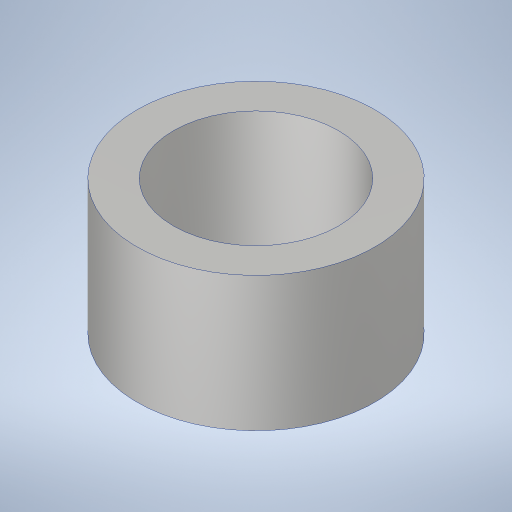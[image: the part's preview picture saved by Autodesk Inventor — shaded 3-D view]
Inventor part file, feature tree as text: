
AUTODESK INVENTOR PART (.ipt)
format: ipt  version: 2023.4 (Build 274418000, 418)  size: 215,552 bytes
history: native  units: in
note: dims shown in document units (in); Inventor stores cm internally (conversion verified against a paired STEP export)
features: extrude x1, sketch x1
ambient origin geometry x8: Origin, YZ Plane, XZ Plane, XY Plane, X Axis, Y Axis, Z Axis, Center Point
bodies: Solid1 (feature_tree)
feature tree (2):
  extrude  "Extrusion1"  Depth=0.444in
  sketch  "Sketch1"  dims[d0=0.785in d1=0.12in d2=0.444in d3=0.0in]
